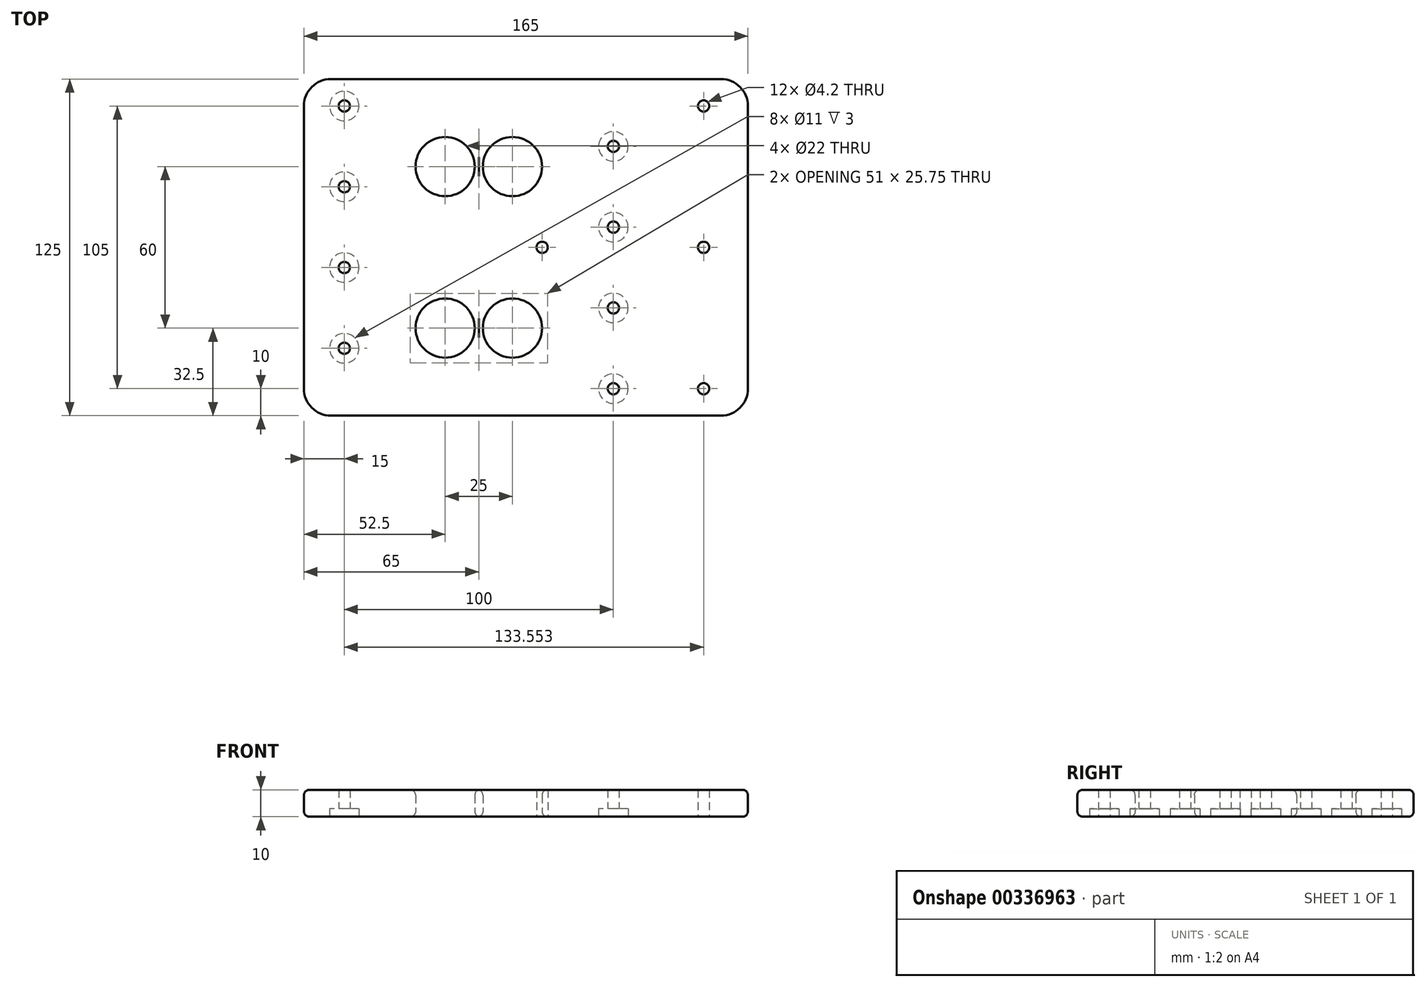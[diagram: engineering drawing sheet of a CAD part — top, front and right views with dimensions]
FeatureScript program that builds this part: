
annotation { "Feature Type Name" : "Feature", "Feature Type Description" : "" }
export const myFeature = defineFeature(function(context is Context, id is Id, definition is map)
    precondition{}
    {
        {
            var Q0;
            Q0=qCreatedBy(makeId("Top.planeOp"),FACE);
            var sketch = newSketch(context, id + "F0", { "sketchPlane" : qUnion([Q0])});
            skCircle(sketch, "E0", {"center": v(15, 25) * mm, "radius": 2.1 * mm});
            skCircle(sketch, "E1.0.1.0", {"center": v(15, 55) * mm, "radius": 2.1 * mm});
            skCircle(sketch, "E1.0.2.0", {"center": v(15, 85) * mm, "radius": 2.1 * mm});
            skCircle(sketch, "E1.0.3.0", {"center": v(15, 115) * mm, "radius": 2.1 * mm});
            skLineSegment(sketch, "E1.direction1", {"start": v(15, 25) * mm, "end": v(115, 25) * mm, "construction": true});
            skLineSegment(sketch, "E1.direction2", {"start": v(15, 25) * mm, "end": v(15, 55) * mm, "construction": true});
            skCircle(sketch, "E2", {"center": v(115, 10) * mm, "radius": 2.1 * mm});
            skCircle(sketch, "E3.0.1.0", {"center": v(115, 40) * mm, "radius": 2.1 * mm});
            skCircle(sketch, "E3.0.2.0", {"center": v(115, 70) * mm, "radius": 2.1 * mm});
            skCircle(sketch, "E3.0.3.0", {"center": v(115, 100) * mm, "radius": 2.1 * mm});
            skLineSegment(sketch, "E3.direction1", {"start": v(115, 10) * mm, "end": v(148.55, 10) * mm, "construction": true});
            skLineSegment(sketch, "E3.direction2", {"start": v(115, 10) * mm, "end": v(115, 40) * mm, "construction": true});
            skLineSegment(sketch, "E4.bottom", {"start": v(0, 0) * mm, "end": v(165, 0) * mm});
            skLineSegment(sketch, "E4.top", {"start": v(0, 125) * mm, "end": v(165, 125) * mm});
            skLineSegment(sketch, "E4.left", {"start": v(0, 0) * mm, "end": v(0, 125) * mm});
            skLineSegment(sketch, "E4.right", {"start": v(165, 0) * mm, "end": v(165, 125) * mm});
            skCircle(sketch, "E5", {"center": v(148.55, 10) * mm, "radius": 2.1 * mm});
            skCircle(sketch, "E6.0.1.0", {"center": v(148.55, 62.5) * mm, "radius": 2.1 * mm});
            skLineSegment(sketch, "E6.direction1", {"start": v(148.55, 10) * mm, "end": v(173.55, 10) * mm, "construction": true});
            skLineSegment(sketch, "E6.direction2", {"start": v(148.55, 10) * mm, "end": v(148.55, 62.5) * mm, "construction": true});
            skCircle(sketch, "E7.0.0.2", {"center": v(148.55, 115) * mm, "radius": 2.1 * mm});
            skCircle(sketch, "E8", {"center": v(52.5, 32.5) * mm, "radius": 11 * mm});
            skCircle(sketch, "E9.0.1.0", {"center": v(52.5, 92.5) * mm, "radius": 11 * mm});
            skCircle(sketch, "E9.1.0.0", {"center": v(77.5, 32.5) * mm, "radius": 11 * mm});
            skCircle(sketch, "E9.1.1.0", {"center": v(77.5, 92.5) * mm, "radius": 11 * mm});
            skLineSegment(sketch, "E9.direction1", {"start": v(52.5, 32.5) * mm, "end": v(77.5, 32.5) * mm, "construction": true});
            skLineSegment(sketch, "E9.direction2", {"start": v(52.5, 32.5) * mm, "end": v(52.5, 92.5) * mm, "construction": true});
            skCircle(sketch, "E10", {"center": v(88.53, 62.5) * mm, "radius": 2.1 * mm});
            skCircle(sketch, "E11", {"center": v(15, 25) * mm, "radius": 5.5 * mm});
            skCircle(sketch, "E12.0.1.0", {"center": v(15, 55) * mm, "radius": 5.5 * mm});
            skCircle(sketch, "E12.0.2.0", {"center": v(15, 85) * mm, "radius": 5.5 * mm});
            skCircle(sketch, "E12.0.3.0", {"center": v(15, 115) * mm, "radius": 5.5 * mm});
            skLineSegment(sketch, "E12.direction1", {"start": v(15, 25) * mm, "end": v(40, 25) * mm, "construction": true});
            skCircle(sketch, "E13", {"center": v(115, 10) * mm, "radius": 5.5 * mm});
            skCircle(sketch, "E14.0.1.0", {"center": v(115, 40) * mm, "radius": 5.5 * mm});
            skCircle(sketch, "E14.0.2.0", {"center": v(115, 70) * mm, "radius": 5.5 * mm});
            skCircle(sketch, "E14.0.3.0", {"center": v(115, 100) * mm, "radius": 5.5 * mm});
            skLineSegment(sketch, "E14.direction1", {"start": v(115, 10) * mm, "end": v(140, 10) * mm, "construction": true});
            skSolve(sketch);
        }
        {
            var Q0;
            Q0=makeQuery(id+"F0.imprint","IMPRINT",FACE,{"disambiguationData":[TD([[makeQuery(id+"F0.imprint","IMPRINT",EDGE,{"derivedFrom":sQuery(id+"F0.wireOp",EDGE,"E4.bottom")}),1.0]])]});
            extrude(context, id + "F1", {"entities" : qUnion([Q0]), "depth" : 10 * mm, "offsetDistance" : 25 * mm});
        }
        {
            var Q0;
            Q0=makeQuery(id+"F0.imprint","IMPRINT",FACE,{"disambiguationData":[TD([[makeQuery(id+"F0.imprint","IMPRINT",EDGE,{"derivedFrom":sQuery(id+"F0.wireOp",EDGE,"E0")}),-1.0]])]});
            var Q1;
            Q1=makeQuery(id+"F0.imprint","IMPRINT",FACE,{"disambiguationData":[TD([[makeQuery(id+"F0.imprint","IMPRINT",EDGE,{"derivedFrom":sQuery(id+"F0.wireOp",EDGE,"E1.0.1.0")}),-1.0]])]});
            var Q2;
            Q2=makeQuery(id+"F0.imprint","IMPRINT",FACE,{"disambiguationData":[TD([[makeQuery(id+"F0.imprint","IMPRINT",EDGE,{"derivedFrom":sQuery(id+"F0.wireOp",EDGE,"E2")}),-1.0]])]});
            var Q3;
            Q3=makeQuery(id+"F0.imprint","IMPRINT",FACE,{"disambiguationData":[TD([[makeQuery(id+"F0.imprint","IMPRINT",EDGE,{"derivedFrom":sQuery(id+"F0.wireOp",EDGE,"E3.0.1.0")}),-1.0]])]});
            var Q4;
            Q4=makeQuery(id+"F0.imprint","IMPRINT",FACE,{"disambiguationData":[TD([[makeQuery(id+"F0.imprint","IMPRINT",EDGE,{"derivedFrom":sQuery(id+"F0.wireOp",EDGE,"E3.0.3.0")}),-1.0]])]});
            var Q5;
            Q5=makeQuery(id+"F0.imprint","IMPRINT",FACE,{"disambiguationData":[TD([[makeQuery(id+"F0.imprint","IMPRINT",EDGE,{"derivedFrom":sQuery(id+"F0.wireOp",EDGE,"E3.0.2.0")}),-1.0]])]});
            var Q6;
            Q6=makeQuery(id+"F0.imprint","IMPRINT",FACE,{"disambiguationData":[TD([[makeQuery(id+"F0.imprint","IMPRINT",EDGE,{"derivedFrom":sQuery(id+"F0.wireOp",EDGE,"E1.0.2.0")}),-1.0]])]});
            var Q7;
            Q7=makeQuery(id+"F0.imprint","IMPRINT",FACE,{"disambiguationData":[TD([[makeQuery(id+"F0.imprint","IMPRINT",EDGE,{"derivedFrom":sQuery(id+"F0.wireOp",EDGE,"E1.0.3.0")}),-1.0]])]});
            extrude(context, id + "F2", {"entities" : qUnion([Q0, Q1, Q2, Q3, Q4, Q5, Q6, Q7]), "operationType" : NewBodyOperationType.ADD, "depth" : 10 * mm, "offsetDistance" : 25 * mm, "hasSecondDirection" : true, "secondDirectionOppositeDirection" : false, "secondDirectionDepth" : 3 * mm});
        }
        {
            var Q0;
            Q0=makeQuery(id+"F1.opExtrude","SWEPT_EDGE",EDGE,{"disambiguationData":[OSD([sQuery(id+"F0.wireOp",EDGE,"E4.bottom"),sQuery(id+"F0.wireOp",EDGE,"E4.right")])]});
            var Q1;
            Q1=makeQuery(id+"F1.opExtrude","SWEPT_EDGE",EDGE,{"disambiguationData":[OSD([sQuery(id+"F0.wireOp",EDGE,"E4.top"),sQuery(id+"F0.wireOp",EDGE,"E4.right")])]});
            var Q2;
            Q2=makeQuery(id+"F1.opExtrude","SWEPT_EDGE",EDGE,{"disambiguationData":[OSD([sQuery(id+"F0.wireOp",EDGE,"E4.top"),sQuery(id+"F0.wireOp",EDGE,"E4.left")])]});
            var Q3;
            Q3=makeQuery(id+"F1.opExtrude","SWEPT_EDGE",EDGE,{"disambiguationData":[OSD([sQuery(id+"F0.wireOp",EDGE,"E4.bottom"),sQuery(id+"F0.wireOp",EDGE,"E4.left")])]});
            fillet(context, id + "F3", {"entities" : qUnion([Q0, Q1, Q2, Q3]), "radius" : 10 * mm, "tangentPropagation" : true, "allowEdgeOverflow" : false});
        }
        {
            var Q0;
            Q0=makeQuery(id+"F1.opExtrude","SWEPT_FACE",FACE,{"disambiguationData":[OSD([sQuery(id+"F0.wireOp",EDGE,"E8")])]});
            var Q1;
            Q1=makeQuery(id+"F1.opExtrude","SWEPT_FACE",FACE,{"disambiguationData":[OSD([sQuery(id+"F0.wireOp",EDGE,"E9.1.0.0")])]});
            var Q2;
            Q2=makeQuery(id+"F1.opExtrude","SWEPT_FACE",FACE,{"disambiguationData":[OSD([sQuery(id+"F0.wireOp",EDGE,"E9.1.1.0")])]});
            var Q3;
            Q3=makeQuery(id+"F1.opExtrude","SWEPT_FACE",FACE,{"disambiguationData":[OSD([sQuery(id+"F0.wireOp",EDGE,"E9.0.1.0")])]});
            var Q4;
            Q4=makeQuery(id+"F1.opExtrude","CAP_EDGE",EDGE,{"disambiguationData":[OSD([sQuery(id+"F0.wireOp",EDGE,"E4.bottom")])],"isStart":false});
            var Q5;
            Q5=makeQuery(id+"F1.opExtrude","CAP_EDGE",EDGE,{"disambiguationData":[OSD([sQuery(id+"F0.wireOp",EDGE,"E4.bottom")])],"isStart":true});
            var Q6;
            Q6=makeQuery(id+"F1.opExtrude","CAP_EDGE",EDGE,{"disambiguationData":[OSD([sQuery(id+"F0.wireOp",EDGE,"E4.left")])],"isStart":false});
            var Q7;
            Q7=makeQuery(id+"F1.opExtrude","CAP_EDGE",EDGE,{"disambiguationData":[OSD([sQuery(id+"F0.wireOp",EDGE,"E4.top")])],"isStart":false});
            var Q8;
            Q8=makeQuery(id+"F1.opExtrude","CAP_EDGE",EDGE,{"disambiguationData":[OSD([sQuery(id+"F0.wireOp",EDGE,"E4.right")])],"isStart":false});
            var Q9;
            Q9=makeQuery(id+"F1.opExtrude","CAP_EDGE",EDGE,{"disambiguationData":[OSD([sQuery(id+"F0.wireOp",EDGE,"E4.right")])],"isStart":true});
            var Q10;
            Q10=makeQuery(id+"F1.opExtrude","CAP_EDGE",EDGE,{"disambiguationData":[OSD([sQuery(id+"F0.wireOp",EDGE,"E4.left")])],"isStart":true});
            var Q11;
            Q11=makeQuery(id+"F1.opExtrude","CAP_EDGE",EDGE,{"disambiguationData":[OSD([sQuery(id+"F0.wireOp",EDGE,"E4.top")])],"isStart":true});
            fillet(context, id + "F4", {"entities" : qUnion([Q0, Q1, Q2, Q3, Q4, Q5, Q6, Q7, Q8, Q9, Q10, Q11]), "radius" : 2 * mm, "tangentPropagation" : true, "allowEdgeOverflow" : false});
        }
    });
